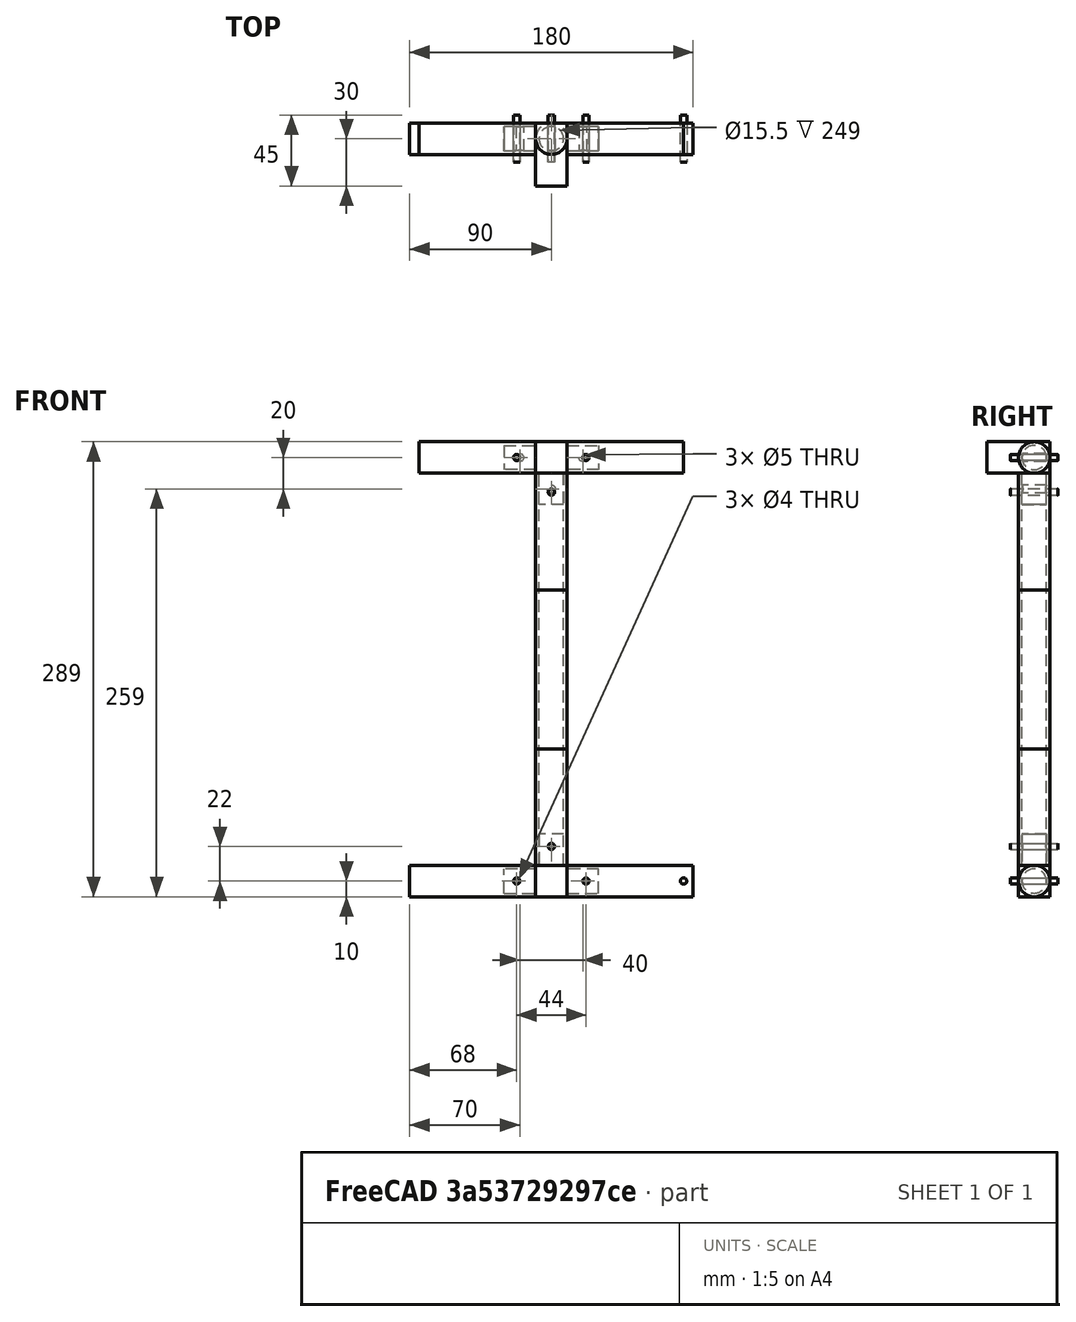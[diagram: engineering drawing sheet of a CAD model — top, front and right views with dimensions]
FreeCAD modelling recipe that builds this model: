
FCSTD DOCUMENT  (FreeCAD 0.21R33771 (Git))
Label: Torso_v2
License: All rights reserved
LicenseURL: http://en.wikipedia.org/wiki/All_rights_reserved
objects: Part::Cylinder×24, Part::MultiFuse×6, App::DocumentObjectGroup×3, Part::Box×2, Part::Cut×2, Part::FeaturePython×1
note: 35 computed .brp shape members not serialized (recipe doc carries the construction recipe); baked Part::Feature solids carry a one-line shape summary decoded from their .brp

FEATURE [Part::Cylinder] Cylinder  label="Cadera_izquierda"
  Angle = 360
  AttacherType = Attacher::AttachEngine3D
  FirstAngle = 0
  Height = 80
  Placement = pos=(10,0,0) rot=(0,1,0;1.5708rad)
  Radius = 10
  SecondAngle = 0
FEATURE [Part::Cylinder] Cylinder002  label="Cadera_dercha"
  Angle = 360
  AttacherType = Attacher::AttachEngine3D
  FirstAngle = 0
  Height = 80
  Placement = pos=(-90,0,0) rot=(0,1,0;1.5708rad)
  Radius = 10
  SecondAngle = 0
FEATURE [Part::Cylinder] Cylinder003  label="Clavicula_derecha"
  Angle = 360
  AttacherType = Attacher::AttachEngine3D
  FirstAngle = 0
  Height = 74
  Placement = pos=(-84,0,269) rot=(0,1,0;1.5708rad)
  Radius = 10
  SecondAngle = 0
FEATURE [Part::Cylinder] Cylinder004  label="Clavicula_izquierda"
  Angle = 360
  AttacherType = Attacher::AttachEngine3D
  FirstAngle = 0
  Height = 74
  Placement = pos=(10,0,269) rot=(0,1,0;1.5708rad)
  Radius = 10
  SecondAngle = 0
FEATURE [Part::Cylinder] Cylinder005  label="Vertebral001"
  Angle = 360
  AttacherType = Attacher::AttachEngine3D
  FirstAngle = 0
  Height = 74
  Placement = pos=(0,0,185) rot=(0,0,1;0rad)
  Radius = 10
  SecondAngle = 0
FEATURE [Part::Cylinder] Cylinder006  label="Vertebral002"
  Angle = 360
  AttacherType = Attacher::AttachEngine3D
  FirstAngle = 0
  Height = 101
  Placement = pos=(0,0,84) rot=(0,0,1;0rad)
  Radius = 10
  SecondAngle = 0
FEATURE [Part::Cylinder] Cylinder007  label="Vertebral003"
  Angle = 360
  AttacherType = Attacher::AttachEngine3D
  FirstAngle = 0
  Height = 74
  Placement = pos=(0,0,10) rot=(0,0,1;0rad)
  Radius = 10
  SecondAngle = 0
FEATURE [Part::Cylinder] Cylinder008  label="Ligamento_cadera"
  Angle = 360
  AttacherType = Attacher::AttachEngine3D
  FirstAngle = 0
  Height = 60
  Placement = pos=(-30,0,0) rot=(0,1,0;1.5708rad)
  Radius = 7.75
  SecondAngle = 0
FEATURE [Part::Cylinder] Cylinder009  label="Ligamento_cadera001"
  Angle = 360
  AttacherType = Attacher::AttachEngine3D
  FirstAngle = 0
  Height = 30
  Radius = 7.75
  SecondAngle = 0
FEATURE [Part::Box] Box  label="Cubo"
  AttacherType = Attacher::AttachEngine3D
  Height = 20
  Length = 20
  Placement = pos=(-10,-10,-10) rot=(0,0,1;0rad)
  Width = 20
FEATURE [Part::FeaturePython] Tube  label="Columna_vertebral"  # WARN: FeaturePython — macro-defined, semantics opaque (R4)
  AttacherType = Attacher::AttachEngine3D
  Height = 249
  InnerRadius = 7.75
  OuterRadius = 10
  Placement = pos=(0,0,10) rot=(0,0,1;0rad)
FEATURE [App::DocumentObjectGroup] Group  label="Tubo_PVC"
  Group = -> [Cylinder,Cylinder002,Cylinder003,Cylinder004,Cylinder005,Cylinder006,Cylinder007,Tube]
FEATURE [Part::Cylinder] Cylinder012  label="Taladros"
  Angle = 360
  AttacherType = Attacher::AttachEngine3D
  FirstAngle = 0
  Height = 30
  Placement = pos=(22,15,0) rot=(1,0,0;1.5708rad)
  Radius = 2
  SecondAngle = 0
FEATURE [Part::Cylinder] Cylinder013  label="Taladros001"
  Angle = 360
  AttacherType = Attacher::AttachEngine3D
  FirstAngle = 0
  Height = 30
  Placement = pos=(-22,15,0) rot=(1,0,0;1.5708rad)
  Radius = 2
  SecondAngle = 0
FEATURE [Part::Cylinder] Cylinder014  label="Taladros002"
  Angle = 360
  AttacherType = Attacher::AttachEngine3D
  FirstAngle = 0
  Height = 30
  Placement = pos=(0,15,22) rot=(1,0,0;1.5708rad)
  Radius = 2
  SecondAngle = 0
FEATURE [Part::MultiFuse] Fusion001  label="Ligamento_T"
  Shapes = -> [Box,Cylinder009,Cylinder008]
FEATURE [Part::MultiFuse] Fusion002  label="Taladros_ligamento_T"
  Shapes = -> [Cylinder014,Cylinder012,Cylinder013]
FEATURE [Part::Cut] Cut  label="Ligamento_T_imprimir"
  Base = -> Fusion001
  Tool = -> Fusion002
FEATURE [App::DocumentObjectGroup] Group001  label="Ligamento_T_cadera"
  Group = -> [Cut]
FEATURE [Part::Box] Box001  label="Cubo001"
  AttacherType = Attacher::AttachEngine3D
  Height = 20
  Length = 20
  Placement = pos=(-10,-10,-10) rot=(0,0,1;0rad)
  Width = 40
FEATURE [Part::Cylinder] Cylinder015  label="Ligamento_cadera002"
  Angle = 360
  AttacherType = Attacher::AttachEngine3D
  FirstAngle = 0
  Height = 60
  Placement = pos=(-30,0,0) rot=(0,1,0;1.5708rad)
  Radius = 7.75
  SecondAngle = 0
FEATURE [Part::Cylinder] Cylinder016  label="Ligamento_cadera003"
  Angle = 360
  AttacherType = Attacher::AttachEngine3D
  FirstAngle = 0
  Height = 30
  Radius = 7.75
  SecondAngle = 0
FEATURE [Part::Cylinder] Cylinder017  label="Taladros003"
  Angle = 360
  AttacherType = Attacher::AttachEngine3D
  FirstAngle = 0
  Height = 30
  Placement = pos=(20,15,0) rot=(1,0,0;1.5708rad)
  Radius = 2.5
  SecondAngle = 0
FEATURE [Part::Cylinder] Cylinder018  label="Taladros004"
  Angle = 360
  AttacherType = Attacher::AttachEngine3D
  FirstAngle = 0
  Height = 30
  Placement = pos=(-20,15,0) rot=(1,0,0;1.5708rad)
  Radius = 2.5
  SecondAngle = 0
FEATURE [Part::Cylinder] Cylinder019  label="Taladros005"
  Angle = 360
  AttacherType = Attacher::AttachEngine3D
  FirstAngle = 0
  Height = 30
  Placement = pos=(0,15,20) rot=(1,0,0;1.5708rad)
  Radius = 2.5
  SecondAngle = 0
FEATURE [Part::MultiFuse] Fusion003  label="Ligamento_T001"
  Shapes = -> [Box001,Cylinder016,Cylinder015]
FEATURE [Part::MultiFuse] Fusion004  label="Taladros_ligamento_T001"
  Shapes = -> [Cylinder019,Cylinder017,Cylinder018]
FEATURE [Part::Cut] Cut001  label="Ligamento_T_imprimir001"
  Base = -> Fusion003
  Placement = pos=(0,0,269) rot=(1,0,0;3.14159rad)
  Tool = -> Fusion004
FEATURE [App::DocumentObjectGroup] Group002  label="Ligamento_T_clavicula"
  Group = -> [Cut001]
FEATURE [Part::Cylinder] Cylinder020  label="Taladros006"
  Angle = 360
  AttacherType = Attacher::AttachEngine3D
  FirstAngle = 0
  Height = 30
  Placement = pos=(22,15,0) rot=(1,0,0;1.5708rad)
  Radius = 2
  SecondAngle = 0
FEATURE [Part::Cylinder] Cylinder021  label="Taladros007"
  Angle = 360
  AttacherType = Attacher::AttachEngine3D
  FirstAngle = 0
  Height = 30
  Placement = pos=(-22,15,0) rot=(1,0,0;1.5708rad)
  Radius = 2
  SecondAngle = 0
FEATURE [Part::Cylinder] Cylinder022  label="Taladros008"
  Angle = 360
  AttacherType = Attacher::AttachEngine3D
  FirstAngle = 0
  Height = 30
  Placement = pos=(0,15,22) rot=(1,0,0;1.5708rad)
  Radius = 2
  SecondAngle = 0
FEATURE [Part::MultiFuse] Fusion005  label="Taladros_ligamento_T002"
  Shapes = -> [Cylinder022,Cylinder020,Cylinder021]
FEATURE [Part::Cylinder] Cylinder023  label="Taladros009"
  Angle = 360
  AttacherType = Attacher::AttachEngine3D
  FirstAngle = 0
  Height = 30
  Placement = pos=(22,15,0) rot=(1,0,0;1.5708rad)
  Radius = 2
  SecondAngle = 0
FEATURE [Part::Cylinder] Cylinder024  label="Taladros010"
  Angle = 360
  AttacherType = Attacher::AttachEngine3D
  FirstAngle = 0
  Height = 30
  Placement = pos=(-22,15,0) rot=(1,0,0;1.5708rad)
  Radius = 2
  SecondAngle = 0
FEATURE [Part::Cylinder] Cylinder025  label="Taladros011"
  Angle = 360
  AttacherType = Attacher::AttachEngine3D
  FirstAngle = 0
  Height = 30
  Placement = pos=(0,15,22) rot=(1,0,0;1.5708rad)
  Radius = 2
  SecondAngle = 0
FEATURE [Part::MultiFuse] Fusion006  label="Taladros_ligamento_T003"
  Placement = pos=(0,0,269) rot=(1,0,0;3.14159rad)
  Shapes = -> [Cylinder025,Cylinder023,Cylinder024]
FEATURE [Part::Cylinder] Cylinder026  label="Taladros012"
  Angle = 360
  AttacherType = Attacher::AttachEngine3D
  FirstAngle = 0
  Height = 30
  Placement = pos=(84,15,0) rot=(1,0,0;1.5708rad)
  Radius = 2
  SecondAngle = 0
